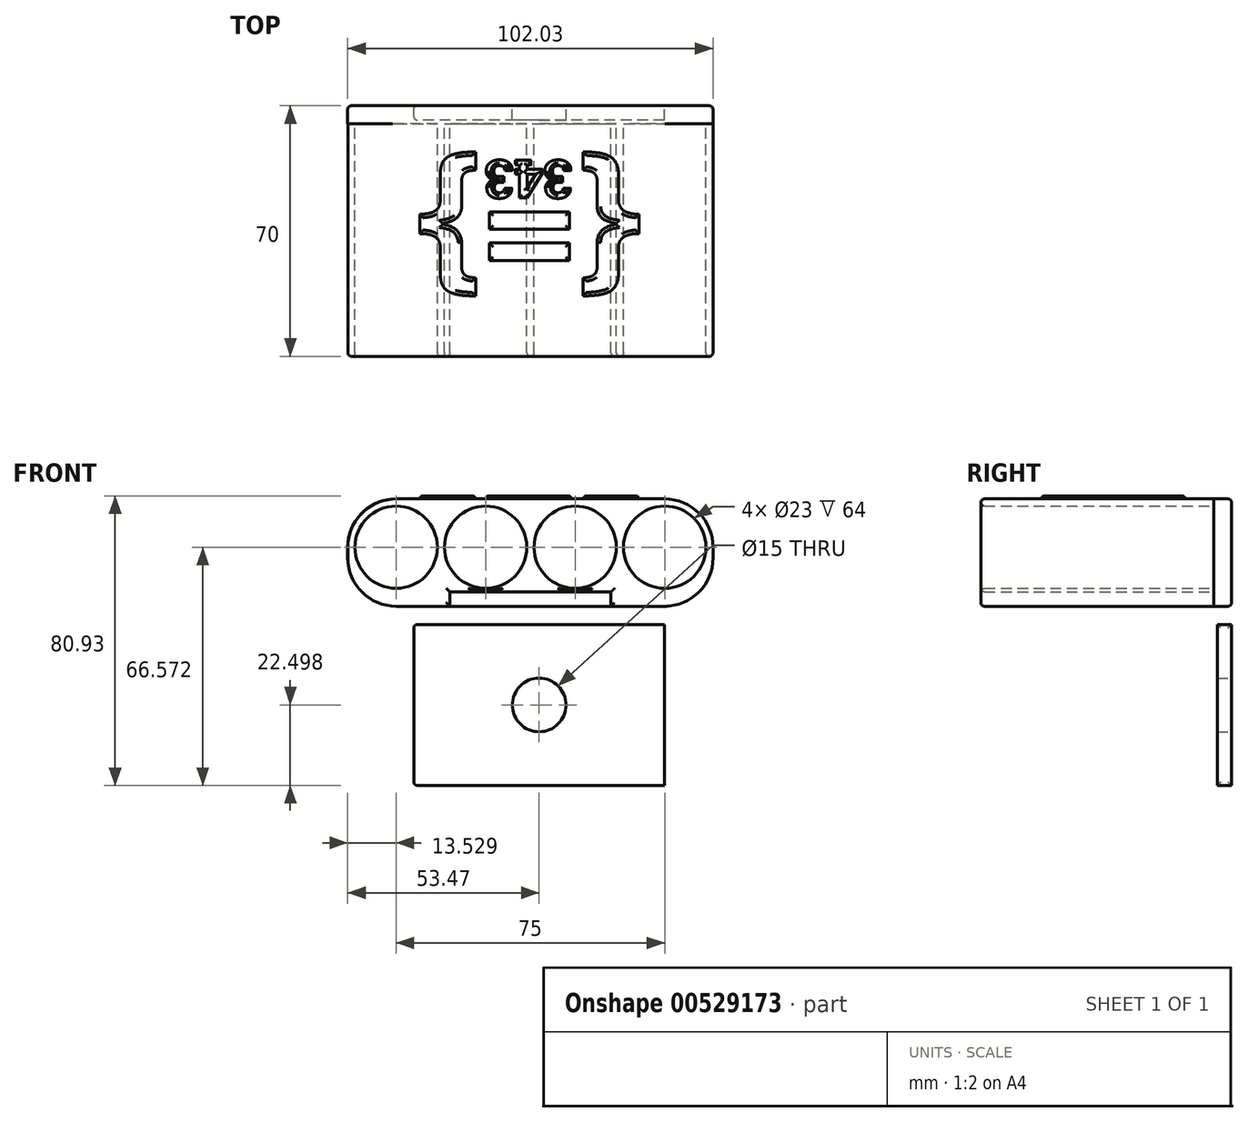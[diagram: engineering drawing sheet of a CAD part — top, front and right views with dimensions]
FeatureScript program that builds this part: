
annotation { "Feature Type Name" : "Feature", "Feature Type Description" : "" }
export const myFeature = defineFeature(function(context is Context, id is Id, definition is map)
    precondition{}
    {
        {
            var Q0;
            Q0=qCreatedBy(makeId("Front.planeOp"),FACE);
            var sketch = newSketch(context, id + "F0", { "sketchPlane" : qUnion([Q0])});
            skLineSegment(sketch, "E0.bottom", {"start": v(-36.23, 25.14) * mm, "end": v(38.77, 25.14) * mm});
            skLineSegment(sketch, "E0.left", {"start": v(-49.73, 11.64) * mm, "end": v(-49.73, 8.64) * mm});
            skLineSegment(sketch, "E0.right", {"start": v(52.27, 11.64) * mm, "end": v(52.27, 8.64) * mm});
            skPoint(sketch, "E1.visualSharp", {"position": v(-49.73, 25.14) * mm});
            skArc(sketch, "E1.filletArc", {"start": v(-36.23, 25.14) * mm, "mid": v(-45.78, 21.19) * mm, "end": v(-49.73, 11.64) * mm});
            skPoint(sketch, "E2.visualSharp", {"position": v(-49.73, -4.86) * mm});
            skArc(sketch, "E2.filletArc", {"start": v(-49.73, 8.64) * mm, "mid": v(-45.78, -0.9) * mm, "end": v(-36.23, -4.86) * mm});
            skPoint(sketch, "E3.visualSharp", {"position": v(52.27, 25.14) * mm});
            skArc(sketch, "E3.filletArc", {"start": v(52.27, 11.64) * mm, "mid": v(48.31, 21.19) * mm, "end": v(38.77, 25.14) * mm});
            skPoint(sketch, "E4.visualSharp", {"position": v(52.27, -4.86) * mm});
            skArc(sketch, "E4.filletArc", {"start": v(38.77, -4.86) * mm, "mid": v(48.31, -0.9) * mm, "end": v(52.27, 8.64) * mm});
            skCircle(sketch, "E5", {"center": v(-36.23, 11.64) * mm, "radius": 11.5 * mm});
            skCircle(sketch, "E6.1.0.0", {"center": v(-11.23, 11.64) * mm, "radius": 11.5 * mm});
            skCircle(sketch, "E6.2.0.0", {"center": v(13.77, 11.64) * mm, "radius": 11.5 * mm});
            skCircle(sketch, "E6.3.0.0", {"center": v(38.77, 11.64) * mm, "radius": 11.5 * mm});
            skLineSegment(sketch, "E6.direction1", {"start": v(-36.23, 11.64) * mm, "end": v(-11.23, 11.64) * mm, "construction": true});
            skLineSegment(sketch, "E7.bottom", {"start": v(-21.23, -0.86) * mm, "end": v(23.77, -0.86) * mm});
            skLineSegment(sketch, "E7.left", {"start": v(-21.23, -0.86) * mm, "end": v(-21.23, -4.86) * mm});
            skLineSegment(sketch, "E7.right", {"start": v(23.77, -0.86) * mm, "end": v(23.77, -4.86) * mm});
            skLineSegment(sketch, "E8", {"start": v(23.77, -4.86) * mm, "end": v(38.77, -4.86) * mm});
            skLineSegment(sketch, "E9", {"start": v(-36.23, -4.86) * mm, "end": v(-21.23, -4.86) * mm});
            skSolve(sketch);
        }
        {
            var Q0;
            Q0 = qSketchRegion(id + "F0", true);
            extrude(context, id + "F1", {"entities" : qUnion([Q0]), "depth" : 70 * mm, "offsetDistance" : 25 * mm, "hasSecondDirection" : true, "secondDirectionOppositeDirection" : false, "secondDirectionDepth" : 5 * mm});
        }
        {
            var Q0;
            Q0=qCreatedBy(makeId("Front.planeOp"),FACE);
            var sketch = newSketch(context, id + "F2", { "sketchPlane" : qUnion([Q0])});
            skLineSegment(sketch, "E10.bottom", {"start": v(-36.26, 25.14) * mm, "end": v(38.74, 25.14) * mm});
            skLineSegment(sketch, "E10.top", {"start": v(-36.26, -4.86) * mm, "end": v(38.74, -4.86) * mm});
            skLineSegment(sketch, "E10.left", {"start": v(-49.76, 11.64) * mm, "end": v(-49.76, 8.64) * mm});
            skLineSegment(sketch, "E10.right", {"start": v(52.24, 11.64) * mm, "end": v(52.24, 8.64) * mm});
            skPoint(sketch, "E11.visualSharp", {"position": v(-49.76, 25.14) * mm});
            skArc(sketch, "E11.filletArc", {"start": v(-36.26, 25.14) * mm, "mid": v(-45.8, 21.19) * mm, "end": v(-49.76, 11.64) * mm});
            skPoint(sketch, "E12.visualSharp", {"position": v(-49.76, -4.86) * mm});
            skArc(sketch, "E12.filletArc", {"start": v(-49.76, 8.64) * mm, "mid": v(-45.8, -0.9) * mm, "end": v(-36.26, -4.86) * mm});
            skPoint(sketch, "E13.visualSharp", {"position": v(52.24, -4.86) * mm});
            skArc(sketch, "E13.filletArc", {"start": v(38.74, -4.86) * mm, "mid": v(48.28, -0.9) * mm, "end": v(52.24, 8.64) * mm});
            skPoint(sketch, "E14.visualSharp", {"position": v(52.24, 25.14) * mm});
            skArc(sketch, "E14.filletArc", {"start": v(52.24, 11.64) * mm, "mid": v(48.28, 21.19) * mm, "end": v(38.74, 25.14) * mm});
            skSolve(sketch);
        }
        {
            var Q0;
            Q0 = qSketchRegion(id + "F2", true);
            extrude(context, id + "F3", {"entities" : qUnion([Q0]), "operationType" : NewBodyOperationType.ADD, "depth" : 5 * mm, "offsetDistance" : 25 * mm});
        }
        {
            var Q0;
            Q0=qCreatedBy(makeId("Front.planeOp"),FACE);
            var sketch = newSketch(context, id + "F4", { "sketchPlane" : qUnion([Q0])});
            skLineSegment(sketch, "E15.bottom", {"start": v(-23.94, -0.85) * mm, "end": v(26.06, -0.85) * mm});
            skLineSegment(sketch, "E15.top", {"start": v(-23.94, -4.85) * mm, "end": v(26.06, -4.85) * mm});
            skLineSegment(sketch, "E15.left", {"start": v(-23.94, -0.85) * mm, "end": v(-23.94, -4.85) * mm});
            skLineSegment(sketch, "E15.right", {"start": v(26.06, -0.85) * mm, "end": v(26.06, -4.85) * mm});
            skSolve(sketch);
        }
        {
            var Q0;
            Q0=qCreatedBy(makeId("Front.planeOp"),FACE);
            var sketch = newSketch(context, id + "F5", { "sketchPlane" : qUnion([Q0])});
            skLineSegment(sketch, "E16.bottom", {"start": v(38.71, -9.93) * mm, "end": v(38.71, -54.93) * mm});
            skLineSegment(sketch, "E16.top", {"start": v(-31.29, -9.93) * mm, "end": v(-31.29, -54.93) * mm});
            skLineSegment(sketch, "E16.left", {"start": v(38.71, -9.93) * mm, "end": v(-31.29, -9.93) * mm});
            skLineSegment(sketch, "E16.right", {"start": v(38.71, -54.93) * mm, "end": v(-31.29, -54.93) * mm});
            skPoint(sketch, "E17", {"position": v(3.71, -32.43) * mm});
            skSolve(sketch);
        }
        {
            var Q0;
            Q0 = qSketchRegion(id + "F5", true);
            extrude(context, id + "F6", {"entities" : qUnion([Q0]), "depth" : 4 * mm, "offsetDistance" : 25 * mm});
        }
        {
            var Q0;
            Q0=qCreatedBy(makeId("Top.planeOp"),FACE);
            var sketch = newSketch(context, id + "F7", { "sketchPlane" : qUnion([Q0])});
            skText(sketch, "E18", { "text": "{=}", "fontName": "OpenSans-Bold.ttf"});
            skText(sketch, "E19", { "text": "343", "fontName": "RobotoSlab-Bold.ttf"});
            const initialGuessF7  = {"E18": [0.03232, -0.0202, -1, 0, 0.03322], "E19": [0.013, -0.01524, -1, 0, 0.01067]};
            skSetInitialGuess(sketch, initialGuessF7);
            skSolve(sketch);
        }
        {
            var Q0;
            Q0 = qSketchRegion(id + "F7", true);
            extrude(context, id + "F8", {"entities" : qUnion([Q0]), "operationType" : NewBodyOperationType.ADD, "depth" : 26 * mm, "offsetDistance" : 25 * mm, "hasSecondDirection" : true, "secondDirectionOppositeDirection" : false, "secondDirectionDepth" : 25 * mm});
        }
        {
            var Q0;
            Q0=sQuery(id+"F5.wireOp",VERTEX,"E17");
            var Q1;
            Q1=makeQuery(id+"F6.opExtrude","SWEPT_BODY",BODY,{"disambiguationData":[OSD([sQuery(id+"F5.wireOp",EDGE,"E16.bottom"),sQuery(id+"F5.wireOp",EDGE,"E16.top"),sQuery(id+"F5.wireOp",EDGE,"E16.left"),sQuery(id+"F5.wireOp",EDGE,"E16.right")])]});
            hole(context, id + "F9", {"style" : HoleStyle.SIMPLE, "endStyle" : HoleEndStyle.THROUGH, "oppositeDirection" : true, "holeDiameter" : 15 * mm, "isTappedThrough" : true, "tappedDepth" : 12 * mm, "tapClearance" : 3, "locations" : qUnion([Q0]), "scope" : qUnion([Q1])});
        }
        {
            var Q0;
            Q0=makeQuery(id+"F1.opExtrude","CAP_FACE",FACE,{"disambiguationData":[OSD([sQuery(id+"F0.wireOp",EDGE,"E5"),sQuery(id+"F0.wireOp",EDGE,"E6.1.0.0"),sQuery(id+"F0.wireOp",EDGE,"E6.2.0.0"),sQuery(id+"F0.wireOp",EDGE,"E6.3.0.0"),sQuery(id+"F0.wireOp",EDGE,"E0.bottom"),sQuery(id+"F0.wireOp",EDGE,"E0.left"),sQuery(id+"F0.wireOp",EDGE,"E0.right"),sQuery(id+"F0.wireOp",EDGE,"E1.filletArc"),sQuery(id+"F0.wireOp",EDGE,"E2.filletArc"),sQuery(id+"F0.wireOp",EDGE,"E3.filletArc"),sQuery(id+"F0.wireOp",EDGE,"E4.filletArc"),sQuery(id+"F0.wireOp",EDGE,"E7.bottom"),sQuery(id+"F0.wireOp",EDGE,"E7.left"),sQuery(id+"F0.wireOp",EDGE,"E7.right"),sQuery(id+"F0.wireOp",EDGE,"E8"),sQuery(id+"F0.wireOp",EDGE,"E9")])],"isStart":false});
            var Q1;
            Q1=makeQuery(id+"F6.opExtrude","SWEPT_FACE",FACE,{"disambiguationData":[OSD([sQuery(id+"F5.wireOp",EDGE,"E16.top")])]});
            var Q2;
            Q2=makeQuery(id+"F3.opExtrude","CAP_FACE",FACE,{"disambiguationData":[OSD([sQuery(id+"F2.wireOp",EDGE,"E10.bottom"),sQuery(id+"F2.wireOp",EDGE,"E10.top"),sQuery(id+"F2.wireOp",EDGE,"E10.left"),sQuery(id+"F2.wireOp",EDGE,"E10.right"),sQuery(id+"F2.wireOp",EDGE,"E11.filletArc"),sQuery(id+"F2.wireOp",EDGE,"E12.filletArc"),sQuery(id+"F2.wireOp",EDGE,"E13.filletArc"),sQuery(id+"F2.wireOp",EDGE,"E14.filletArc")])],"isStart":true});
            var Q3;
            Q3=makeQuery(id+"F8.opExtrude","CAP_FACE",FACE,{"disambiguationData":[OSD([sQuery(id+"F7.wireOp",EDGE,"E18.sketch_text.stroke-0"),sQuery(id+"F7.wireOp",EDGE,"E18.sketch_text.stroke-1"),sQuery(id+"F7.wireOp",EDGE,"E18.sketch_text.stroke-2"),sQuery(id+"F7.wireOp",EDGE,"E18.sketch_text.stroke-3"),sQuery(id+"F7.wireOp",EDGE,"E18.sketch_text.stroke-4"),sQuery(id+"F7.wireOp",EDGE,"E18.sketch_text.stroke-5"),sQuery(id+"F7.wireOp",EDGE,"E18.sketch_text.stroke-6"),sQuery(id+"F7.wireOp",EDGE,"E18.sketch_text.stroke-7"),sQuery(id+"F7.wireOp",EDGE,"E18.sketch_text.stroke-8"),sQuery(id+"F7.wireOp",EDGE,"E18.sketch_text.stroke-9"),sQuery(id+"F7.wireOp",EDGE,"E18.sketch_text.stroke-10"),sQuery(id+"F7.wireOp",EDGE,"E18.sketch_text.stroke-11"),sQuery(id+"F7.wireOp",EDGE,"E18.sketch_text.stroke-12"),sQuery(id+"F7.wireOp",EDGE,"E18.sketch_text.stroke-13"),sQuery(id+"F7.wireOp",EDGE,"E18.sketch_text.stroke-14"),sQuery(id+"F7.wireOp",EDGE,"E18.sketch_text.stroke-15"),sQuery(id+"F7.wireOp",EDGE,"E18.sketch_text.stroke-16"),sQuery(id+"F7.wireOp",EDGE,"E18.sketch_text.stroke-17"),sQuery(id+"F7.wireOp",EDGE,"E18.sketch_text.stroke-18"),sQuery(id+"F7.wireOp",EDGE,"E18.sketch_text.stroke-19"),sQuery(id+"F7.wireOp",EDGE,"E18.sketch_text.stroke-20"),sQuery(id+"F7.wireOp",EDGE,"E18.sketch_text.stroke-21"),sQuery(id+"F7.wireOp",EDGE,"E18.sketch_text.stroke-22"),sQuery(id+"F7.wireOp",EDGE,"E18.sketch_text.stroke-23")])],"isStart":false});
            var Q4;
            Q4=makeQuery(id+"F8.opExtrude","CAP_FACE",FACE,{"disambiguationData":[OSD([sQuery(id+"F7.wireOp",EDGE,"E18.sketch_text.stroke-24"),sQuery(id+"F7.wireOp",EDGE,"E18.sketch_text.stroke-25"),sQuery(id+"F7.wireOp",EDGE,"E18.sketch_text.stroke-26"),sQuery(id+"F7.wireOp",EDGE,"E18.sketch_text.stroke-27")])],"isStart":false});
            var Q5;
            Q5=makeQuery(id+"F8.opExtrude","CAP_FACE",FACE,{"disambiguationData":[OSD([sQuery(id+"F7.wireOp",EDGE,"E18.sketch_text.stroke-28"),sQuery(id+"F7.wireOp",EDGE,"E18.sketch_text.stroke-29"),sQuery(id+"F7.wireOp",EDGE,"E18.sketch_text.stroke-30"),sQuery(id+"F7.wireOp",EDGE,"E18.sketch_text.stroke-31")])],"isStart":false});
            var Q6;
            Q6=makeQuery(id+"F8.opExtrude","CAP_FACE",FACE,{"disambiguationData":[OSD([sQuery(id+"F7.wireOp",EDGE,"E18.sketch_text.stroke-32"),sQuery(id+"F7.wireOp",EDGE,"E18.sketch_text.stroke-33"),sQuery(id+"F7.wireOp",EDGE,"E18.sketch_text.stroke-34"),sQuery(id+"F7.wireOp",EDGE,"E18.sketch_text.stroke-35"),sQuery(id+"F7.wireOp",EDGE,"E18.sketch_text.stroke-36"),sQuery(id+"F7.wireOp",EDGE,"E18.sketch_text.stroke-37"),sQuery(id+"F7.wireOp",EDGE,"E18.sketch_text.stroke-38"),sQuery(id+"F7.wireOp",EDGE,"E18.sketch_text.stroke-39"),sQuery(id+"F7.wireOp",EDGE,"E18.sketch_text.stroke-40"),sQuery(id+"F7.wireOp",EDGE,"E18.sketch_text.stroke-41"),sQuery(id+"F7.wireOp",EDGE,"E18.sketch_text.stroke-42"),sQuery(id+"F7.wireOp",EDGE,"E18.sketch_text.stroke-43"),sQuery(id+"F7.wireOp",EDGE,"E18.sketch_text.stroke-44"),sQuery(id+"F7.wireOp",EDGE,"E18.sketch_text.stroke-45"),sQuery(id+"F7.wireOp",EDGE,"E18.sketch_text.stroke-46"),sQuery(id+"F7.wireOp",EDGE,"E18.sketch_text.stroke-47"),sQuery(id+"F7.wireOp",EDGE,"E18.sketch_text.stroke-48"),sQuery(id+"F7.wireOp",EDGE,"E18.sketch_text.stroke-49"),sQuery(id+"F7.wireOp",EDGE,"E18.sketch_text.stroke-50"),sQuery(id+"F7.wireOp",EDGE,"E18.sketch_text.stroke-51"),sQuery(id+"F7.wireOp",EDGE,"E18.sketch_text.stroke-52"),sQuery(id+"F7.wireOp",EDGE,"E18.sketch_text.stroke-53"),sQuery(id+"F7.wireOp",EDGE,"E18.sketch_text.stroke-54"),sQuery(id+"F7.wireOp",EDGE,"E18.sketch_text.stroke-55"),sQuery(id+"F7.wireOp",EDGE,"E18.sketch_text.stroke-56"),sQuery(id+"F7.wireOp",EDGE,"E18.sketch_text.stroke-57"),sQuery(id+"F7.wireOp",EDGE,"E18.sketch_text.stroke-58")])],"isStart":false});
            fillet(context, id + "F10", {"entities" : qUnion([Q0, Q1, Q2, Q3, Q4, Q5, Q6]), "radius" : 1 * mm, "tangentPropagation" : true, "allowEdgeOverflow" : false});
        }
        {
            var Q0;
            Q0=makeQuery(id+"F8.opExtrude","CAP_FACE",FACE,{"disambiguationData":[OSD([sQuery(id+"F7.wireOp",EDGE,"E19.sketch_text.stroke-0"),sQuery(id+"F7.wireOp",EDGE,"E19.sketch_text.stroke-1"),sQuery(id+"F7.wireOp",EDGE,"E19.sketch_text.stroke-2"),sQuery(id+"F7.wireOp",EDGE,"E19.sketch_text.stroke-3"),sQuery(id+"F7.wireOp",EDGE,"E19.sketch_text.stroke-4"),sQuery(id+"F7.wireOp",EDGE,"E19.sketch_text.stroke-5"),sQuery(id+"F7.wireOp",EDGE,"E19.sketch_text.stroke-6"),sQuery(id+"F7.wireOp",EDGE,"E19.sketch_text.stroke-7"),sQuery(id+"F7.wireOp",EDGE,"E19.sketch_text.stroke-8"),sQuery(id+"F7.wireOp",EDGE,"E19.sketch_text.stroke-9"),sQuery(id+"F7.wireOp",EDGE,"E19.sketch_text.stroke-10"),sQuery(id+"F7.wireOp",EDGE,"E19.sketch_text.stroke-11"),sQuery(id+"F7.wireOp",EDGE,"E19.sketch_text.stroke-12"),sQuery(id+"F7.wireOp",EDGE,"E19.sketch_text.stroke-13"),sQuery(id+"F7.wireOp",EDGE,"E19.sketch_text.stroke-14"),sQuery(id+"F7.wireOp",EDGE,"E19.sketch_text.stroke-15"),sQuery(id+"F7.wireOp",EDGE,"E19.sketch_text.stroke-16"),sQuery(id+"F7.wireOp",EDGE,"E19.sketch_text.stroke-17"),sQuery(id+"F7.wireOp",EDGE,"E19.sketch_text.stroke-18"),sQuery(id+"F7.wireOp",EDGE,"E19.sketch_text.stroke-19"),sQuery(id+"F7.wireOp",EDGE,"E19.sketch_text.stroke-20"),sQuery(id+"F7.wireOp",EDGE,"E19.sketch_text.stroke-21"),sQuery(id+"F7.wireOp",EDGE,"E19.sketch_text.stroke-22"),sQuery(id+"F7.wireOp",EDGE,"E19.sketch_text.stroke-23"),sQuery(id+"F7.wireOp",EDGE,"E19.sketch_text.stroke-24"),sQuery(id+"F7.wireOp",EDGE,"E19.sketch_text.stroke-25"),sQuery(id+"F7.wireOp",EDGE,"E19.sketch_text.stroke-26"),sQuery(id+"F7.wireOp",EDGE,"E19.sketch_text.stroke-27"),sQuery(id+"F7.wireOp",EDGE,"E19.sketch_text.stroke-28"),sQuery(id+"F7.wireOp",EDGE,"E19.sketch_text.stroke-29"),sQuery(id+"F7.wireOp",EDGE,"E19.sketch_text.stroke-30")])],"isStart":false});
            var Q1;
            Q1=makeQuery(id+"F8.opExtrude","CAP_FACE",FACE,{"disambiguationData":[OSD([sQuery(id+"F7.wireOp",EDGE,"E19.sketch_text.stroke-51"),sQuery(id+"F7.wireOp",EDGE,"E19.sketch_text.stroke-52"),sQuery(id+"F7.wireOp",EDGE,"E19.sketch_text.stroke-53"),sQuery(id+"F7.wireOp",EDGE,"E19.sketch_text.stroke-54"),sQuery(id+"F7.wireOp",EDGE,"E19.sketch_text.stroke-55"),sQuery(id+"F7.wireOp",EDGE,"E19.sketch_text.stroke-56"),sQuery(id+"F7.wireOp",EDGE,"E19.sketch_text.stroke-57"),sQuery(id+"F7.wireOp",EDGE,"E19.sketch_text.stroke-58"),sQuery(id+"F7.wireOp",EDGE,"E19.sketch_text.stroke-59"),sQuery(id+"F7.wireOp",EDGE,"E19.sketch_text.stroke-60"),sQuery(id+"F7.wireOp",EDGE,"E19.sketch_text.stroke-61"),sQuery(id+"F7.wireOp",EDGE,"E19.sketch_text.stroke-62"),sQuery(id+"F7.wireOp",EDGE,"E19.sketch_text.stroke-63"),sQuery(id+"F7.wireOp",EDGE,"E19.sketch_text.stroke-64"),sQuery(id+"F7.wireOp",EDGE,"E19.sketch_text.stroke-65"),sQuery(id+"F7.wireOp",EDGE,"E19.sketch_text.stroke-66"),sQuery(id+"F7.wireOp",EDGE,"E19.sketch_text.stroke-67"),sQuery(id+"F7.wireOp",EDGE,"E19.sketch_text.stroke-68"),sQuery(id+"F7.wireOp",EDGE,"E19.sketch_text.stroke-69"),sQuery(id+"F7.wireOp",EDGE,"E19.sketch_text.stroke-70"),sQuery(id+"F7.wireOp",EDGE,"E19.sketch_text.stroke-71"),sQuery(id+"F7.wireOp",EDGE,"E19.sketch_text.stroke-72"),sQuery(id+"F7.wireOp",EDGE,"E19.sketch_text.stroke-73"),sQuery(id+"F7.wireOp",EDGE,"E19.sketch_text.stroke-74"),sQuery(id+"F7.wireOp",EDGE,"E19.sketch_text.stroke-75"),sQuery(id+"F7.wireOp",EDGE,"E19.sketch_text.stroke-76"),sQuery(id+"F7.wireOp",EDGE,"E19.sketch_text.stroke-77"),sQuery(id+"F7.wireOp",EDGE,"E19.sketch_text.stroke-78"),sQuery(id+"F7.wireOp",EDGE,"E19.sketch_text.stroke-79"),sQuery(id+"F7.wireOp",EDGE,"E19.sketch_text.stroke-80"),sQuery(id+"F7.wireOp",EDGE,"E19.sketch_text.stroke-81")])],"isStart":false});
            var Q2;
            Q2=makeQuery(id+"F8.opExtrude","CAP_FACE",FACE,{"disambiguationData":[OSD([sQuery(id+"F7.wireOp",EDGE,"E19.sketch_text.stroke-31"),sQuery(id+"F7.wireOp",EDGE,"E19.sketch_text.stroke-32"),sQuery(id+"F7.wireOp",EDGE,"E19.sketch_text.stroke-33"),sQuery(id+"F7.wireOp",EDGE,"E19.sketch_text.stroke-34"),sQuery(id+"F7.wireOp",EDGE,"E19.sketch_text.stroke-35"),sQuery(id+"F7.wireOp",EDGE,"E19.sketch_text.stroke-36"),sQuery(id+"F7.wireOp",EDGE,"E19.sketch_text.stroke-37"),sQuery(id+"F7.wireOp",EDGE,"E19.sketch_text.stroke-38"),sQuery(id+"F7.wireOp",EDGE,"E19.sketch_text.stroke-39"),sQuery(id+"F7.wireOp",EDGE,"E19.sketch_text.stroke-40"),sQuery(id+"F7.wireOp",EDGE,"E19.sketch_text.stroke-41"),sQuery(id+"F7.wireOp",EDGE,"E19.sketch_text.stroke-42"),sQuery(id+"F7.wireOp",EDGE,"E19.sketch_text.stroke-43"),sQuery(id+"F7.wireOp",EDGE,"E19.sketch_text.stroke-44"),sQuery(id+"F7.wireOp",EDGE,"E19.sketch_text.stroke-45"),sQuery(id+"F7.wireOp",EDGE,"E19.sketch_text.stroke-46"),sQuery(id+"F7.wireOp",EDGE,"E19.sketch_text.stroke-47"),sQuery(id+"F7.wireOp",EDGE,"E19.sketch_text.stroke-48"),sQuery(id+"F7.wireOp",EDGE,"E19.sketch_text.stroke-49"),sQuery(id+"F7.wireOp",EDGE,"E19.sketch_text.stroke-50")])],"isStart":false});
            fillet(context, id + "F11", {"entities" : qUnion([Q0, Q1, Q2]), "radius" : 0.7 * mm, "tangentPropagation" : true, "allowEdgeOverflow" : false});
        }
    });
